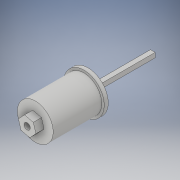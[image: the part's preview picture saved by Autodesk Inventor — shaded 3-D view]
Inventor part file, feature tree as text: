
AUTODESK INVENTOR PART (.ipt)
format: ipt  version: 2018 (Build 220112000, 112)  size: 131,072 bytes
history: native  units: in
note: dims shown in document units (in); Inventor stores cm internally (conversion verified against a paired STEP export)
features: sketch x6, extrude x5
ambient origin geometry x8: Origin, YZ Plane, XZ Plane, XY Plane, X Axis, Y Axis, Z Axis, Center Point
bodies: Solid1 (feature_tree)
feature tree (11):
  extrude  "Extrusion1"  Depth=0.125in TaperAngle=0.0deg
  extrude  "Extrusion2"  Depth=1.5in TaperAngle=0.0deg
  extrude  "Extrusion3"  Depth=0.25in TaperAngle=0.0deg
  extrude  "Extrusion4"  Depth=0.75in TaperAngle=0.0deg
  extrude  "Extrusion5"  Depth=2.0in TaperAngle=0.0deg
  sketch  "Sketch6"
  sketch  "Sketch1"  dims[d0=1.25in d1=0.125in d2=0.0in]
  sketch  "Sketch2"  dims[d3=1.105in d4=1.5in d5=0.0in]
  sketch  "Sketch3"  dims[d6=0.48in d7=0.25in d8=0.0in]
  sketch  "Sketch4"  dims[d9=0.193in d10=0.75in d11=0.0in]
  sketch  "Sketch5"  dims[d12=0.145in d13=2.0in d14=0.0in]
